# Revit family: Rheem - Aquaheat 270L
name_source: partatom
category: Mechanical Equipment
units: mm (PartAtom-declared; Revit-internal decimal feet)

## family parameters
Always vertical = Yes
Classification = None
Cut with Voids When Loaded = No
Part Type = Normal
Room Calculation Point = No
Round Connector Dimension = Use Diameter
Shared = No
Work Plane-Based = No

## types (1)
- Rheem - Aquaheat 270L
    Cable Entry Height = 274 mm  [stored 0.89895 ft]
    Capacity = 270.0 L
    Default Elevation = 0 mm  [stored 0 ft]
    Description = Rheem Aquaheat HDc-270 Heat Pumo
    Diameter = 720 mm  [stored 2.3622 ft]
    Height = 1825 mm  [stored 5.98753 ft]
    Manufacturer = Rheem
    Minimum Clearance Wall 1 = 350 mm  [stored 1.14829 ft]
    Minimum Clearance Wall 2 = 1000 mm  [stored 3.28084 ft]
    Minimum Clearance Wall Back = 25 mm  [stored 0.082021 ft]
    Model = Ambiheat HDc-270
    Recommended Wall Clearance 1 = 900 mm  [stored 2.95276 ft]
    URL = https://rheem.co.nz

note: [stored X ft] marks values corroborated as IEEE doubles in the binary element streams (Revit-internal decimal feet)

## geometry (parser evidence)
native form markers: Revolve x1, Sweep x1
no freeform markers — native parametric forms only
